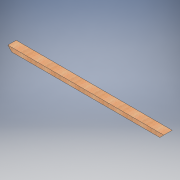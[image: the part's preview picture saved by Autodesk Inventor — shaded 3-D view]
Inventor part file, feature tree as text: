
AUTODESK INVENTOR PART (.ipt)
format: ipt  version: 2016 (Build 200138000, 138)  size: 98,816 bytes
history: native  units: in
note: dims shown in document units (in); Inventor stores cm internally (conversion verified against a paired STEP export)
features: extrude x1, sketch x1
ambient origin geometry x8: Origin, YZ Plane, XZ Plane, XY Plane, X Axis, Y Axis, Z Axis, Center Point
bodies: Body1 (feature_tree)
feature tree (2):
  extrude  "Extrusion2"  TaperAngle=135.0deg  [1 undecoded]
  sketch  "Sketch2"  dims[d10=45.0deg d11=135.0deg d12=3.5in d13=0.0in d14=65.0in]
note: 1 required parameter value undecoded (feature->parameter linkage not recoverable at this tier; creation-order binding heuristic only, values carry confidence <= 0.55)
